# Revit family: Hager-UNIVERS-Surface_mounted-IP44-With_Cover-With_DIN-NoHosted-DE-de
name_source: partatom
category: Electrical Equipment
units: mm (PartAtom-declared; Revit-internal decimal feet)

## family parameters
Always vertical = Yes
Cut with Voids When Loaded = No
Maintain Annotation Orientation = No
Panel Configuration = Two Columns, Circuits Across
Part Type = Panelboard
Room Calculation Point = No
Round Connector Dimension = Use Diameter
Shared = No
Work Plane-Based = Yes

## types (114) — shared parameters
Code hager = ADD-EC000214_EU
Default Elevation = 1200 mm
EF000007 - Farbe = weiß
EF000024 - UV-beständig = No
EF000049 - Tiefe = 165 mm
EF000116 - RAL-Nummer = 9010
EF000118 - Mit Montageplatte = No
EF001062 - EMV-Ausführung = No
EF001088 - Anbaumöglichkeit = Yes
EF001134 - DIN-Schiene = Yes
EF004462 - Art der Schließung = sonstige
EF005474 - Schutzart (IP) = IP44
EF006306 - Mit Schloss = No
EF015941 - Signaldurchlassende Tür = No
ETIM class code = EC000214
ETIM class name = Small distribution board
HG000002-Mit tür = Yes
HG000003-Bereich = UNIVERS
HG000005-Dicke = 2 mm  [stored 0.00656168 ft]
HG000006-Flush mounted = No
HG000011-Leere Reihen von unten = No
HG000012-Türschwenkwinkel = 90.00°
HG000013-Tür links = No
HG000014-Tür rechts = Yes
HG000015-Sichtbarkeit der Türöffnung = Yes
HG000016-3D-Türsichtbarkeit = Yes
HG000017-Distanz zwischen den Polen = 18 mm  [stored 0.0590551 ft]
HG000060-RAL-number = 9010
HG000099-Onfly Template ID-de-DE = 507532
Manufacturer = Hager
Name BIM&CO = Electricity
Name hager = ADD_Enclosures_EC000214
Reference = Template-Enclosure_EU-EC000214
Uniformat = Low Tension Service & Dist.
Uniformat code = D501001
zero-valued in all types: EF001131 - Innentiefe

## per-type parameters (varying)
| type | BC_METADATA | EF000003 - Montageart | EF000008 - Breite | EF000040 - Höhe | EF000218 - Einbautiefe | EF000266 - Anzahl der Reihen | EF000332 - Einbauhöhe | EF000846 - Einbaubreite | EF002950 - Breite in Teilungseinheiten | EF006244 - Transparenter Deckel/Tür | EF009212 - Ausführung Deckel | EF015776 - Erdungsklemmenblock | EF015777 - Neutralleiterklemmenblock | HG000001-Anzahl der Spalten | HG000004-Herstellerreferenz | HG000007-Anzahl der leeren Spalten | HG000008-Anzahl der leeren Reihen | HG000009-Doppelflügeligen Tür | HG000010-Asymmetrische Türen | HGEF000266-Anzahl der Reihen | HGEF0002950-Breite in Teilungseinheiten |
| UNIVERS-Surface_mounted_W800_H1100_D165_36_Modular_Spacing-FWB73 | {"ObjectGuid":"4b98beaf-e054-4bb3-81df-89b0e6f75c23","ModelGuid":"5a9c6bb8-e142-4675-a376-75949bd55e93","VariantGuid":"0dd3dc3a-ebdd-402e-9744-e7fcb90a7f47","Revision":"#6","VariantName":"UNIVERS-Surface_mounted_W800_H1100_D165_36_Modular_Spacing-FWB73"} | Aufputz | 800 mm  [stored 2.62467 ft] | 1100 mm | 161 mm  [stored 0.528215 ft] | 7 | 1100 mm | 800 mm  [stored 2.62467 ft] | 36 | No | mit Ausschnitt | No | Yes | 3 | FWB73 | 0 | 0 | Yes | Yes | 7 | 36 |
| UNIVERS-Surface_mounted_W800_H1100_D165_36_Modular_Spacing-FWB73A | {"ObjectGuid":"4b98beaf-e054-4bb3-81df-89b0e6f75c23","ModelGuid":"5a9c6bb8-e142-4675-a376-75949bd55e93","VariantGuid":"f96014db-38ca-47cd-be6b-f56e55ff9696","Revision":"#6","VariantName":"UNIVERS-Surface_mounted_W800_H1100_D165_36_Modular_Spacing-FWB73A"} | Aufputz | 800 mm  [stored 2.62467 ft] | 1100 mm | 161 mm  [stored 0.528215 ft] | 7 | 1100 mm | 800 mm  [stored 2.62467 ft] | 36 | No | mit Ausschnitt | No | No | 3 | FWB73A | 0 | 0 | Yes | Yes | 7 | 36 |
| UNIVERS-Surface_mounted_W800_H1100_D165_36_Modular_Spacing-FWB73GS | {"ObjectGuid":"4b98beaf-e054-4bb3-81df-89b0e6f75c23","ModelGuid":"5a9c6bb8-e142-4675-a376-75949bd55e93","VariantGuid":"dc065a56-8912-4b0e-b599-fcd4edfbecf9","Revision":"#6","VariantName":"UNIVERS-Surface_mounted_W800_H1100_D165_36_Modular_Spacing-FWB73GS"} | Aufputz | 800 mm  [stored 2.62467 ft] | 1100 mm | 161 mm  [stored 0.528215 ft] | 7 | 1100 mm | 800 mm  [stored 2.62467 ft] | 36 | Yes | mit Ausschnitt | Yes | Yes | 3 | FWB73GS | 0 | 0 | Yes | Yes | 7 | 36 |
| UNIVERS-Surface_mounted_W800_H1100_D165_36_Modular_Spacing-FWB73N | {"ObjectGuid":"4b98beaf-e054-4bb3-81df-89b0e6f75c23","ModelGuid":"5a9c6bb8-e142-4675-a376-75949bd55e93","VariantGuid":"0aaa04c3-c58c-4ad2-b219-bbb140eb05cf","Revision":"#6","VariantName":"UNIVERS-Surface_mounted_W800_H1100_D165_36_Modular_Spacing-FWB73N"} | Aufputz | 800 mm  [stored 2.62467 ft] | 1100 mm | 161 mm  [stored 0.528215 ft] | 7 | 1100 mm | 800 mm  [stored 2.62467 ft] | 36 | No | mit Ausschnitt | No | No | 3 | FWB73N | 0 | 2 | Yes | Yes | 7 | 36 |
| UNIVERS-Surface_mounted_W800_H1100_D165_36_Modular_Spacing-FWB73N3 | {"ObjectGuid":"4b98beaf-e054-4bb3-81df-89b0e6f75c23","ModelGuid":"5a9c6bb8-e142-4675-a376-75949bd55e93","VariantGuid":"30b08112-a314-4a2f-b8eb-9d62cf59b380","Revision":"#6","VariantName":"UNIVERS-Surface_mounted_W800_H1100_D165_36_Modular_Spacing-FWB73N3"} | Aufputz | 800 mm  [stored 2.62467 ft] | 1100 mm | 161 mm  [stored 0.528215 ft] | 7 | 1100 mm | 800 mm  [stored 2.62467 ft] | 36 | No | mit Ausschnitt | No | No | 3 | FWB73N3 | 0 | 2 | Yes | Yes | 7 | 36 |
| UNIVERS-Surface_mounted_W800_H1100_D165_36_Modular_Spacing-FWB73S | {"ObjectGuid":"4b98beaf-e054-4bb3-81df-89b0e6f75c23","ModelGuid":"5a9c6bb8-e142-4675-a376-75949bd55e93","VariantGuid":"13865e0f-bc95-4182-ab0f-007a18ae3678","Revision":"#6","VariantName":"UNIVERS-Surface_mounted_W800_H1100_D165_36_Modular_Spacing-FWB73S"} | Aufputz/Unterputz | 800 mm  [stored 2.62467 ft] | 1100 mm | 161 mm  [stored 0.528215 ft] | 7 | 1100 mm | 800 mm  [stored 2.62467 ft] | 36 | No | mit Ausschnitt | Yes | Yes | 3 | FWB73S | 0 | 0 | Yes | Yes | 7 | 36 |
| UNIVERS-Surface_mounted_W1050_H1100_D165_48_Modular_Spacing-FWB74 | {"ObjectGuid":"4b98beaf-e054-4bb3-81df-89b0e6f75c23","ModelGuid":"5a9c6bb8-e142-4675-a376-75949bd55e93","VariantGuid":"79b8c612-cb7d-4498-8013-b0a4b8235b0e","Revision":"#6","VariantName":"UNIVERS-Surface_mounted_W1050_H1100_D165_48_Modular_Spacing-FWB74"} | Aufputz | 1050 mm | 1100 mm | 161 mm  [stored 0.528215 ft] | 7 | 1100 mm | 1050 mm | 48 | No | mit Ausschnitt | No | Yes | 4 | FWB74 | 0 | 0 | Yes | No | 7 | 48 |
| UNIVERS-Surface_mounted_W1050_H1100_D165_48_Modular_Spacing-FWB74A | {"ObjectGuid":"4b98beaf-e054-4bb3-81df-89b0e6f75c23","ModelGuid":"5a9c6bb8-e142-4675-a376-75949bd55e93","VariantGuid":"296b363e-7e7e-4d48-a850-0f3362c6178a","Revision":"#6","VariantName":"UNIVERS-Surface_mounted_W1050_H1100_D165_48_Modular_Spacing-FWB74A"} | Aufputz | 1050 mm | 1100 mm | 161 mm  [stored 0.528215 ft] | 7 | 1100 mm | 1050 mm | 48 | No | mit Ausschnitt | No | No | 4 | FWB74A | 0 | 0 | Yes | No | 7 | 48 |
| UNIVERS-Surface_mounted_W1050_H1100_D165_48_Modular_Spacing-FWB74GS | {"ObjectGuid":"4b98beaf-e054-4bb3-81df-89b0e6f75c23","ModelGuid":"5a9c6bb8-e142-4675-a376-75949bd55e93","VariantGuid":"3207d950-e017-4842-a3d5-3d6932ddf406","Revision":"#6","VariantName":"UNIVERS-Surface_mounted_W1050_H1100_D165_48_Modular_Spacing-FWB74GS"} | Aufputz | 1050 mm | 1100 mm | 161 mm  [stored 0.528215 ft] | 7 | 1100 mm | 1050 mm | 48 | Yes | mit Ausschnitt | Yes | Yes | 4 | FWB74GS | 0 | 0 | Yes | No | 7 | 48 |
| UNIVERS-Surface_mounted_W1050_H1100_D165_48_Modular_Spacing-FWB74N | {"ObjectGuid":"4b98beaf-e054-4bb3-81df-89b0e6f75c23","ModelGuid":"5a9c6bb8-e142-4675-a376-75949bd55e93","VariantGuid":"8fe7d4e4-44c9-485e-808a-0732e1737a3e","Revision":"#6","VariantName":"UNIVERS-Surface_mounted_W1050_H1100_D165_48_Modular_Spacing-FWB74N"} | Aufputz | 1050 mm | 1100 mm | 161 mm  [stored 0.528215 ft] | 7 | 1100 mm | 1050 mm | 48 | No | mit Ausschnitt | No | No | 4 | FWB74N | 0 | 2 | Yes | No | 7 | 48 |
| UNIVERS-Surface_mounted_W1050_H1100_D165_48_Modular_Spacing-FWB74N3 | {"ObjectGuid":"4b98beaf-e054-4bb3-81df-89b0e6f75c23","ModelGuid":"5a9c6bb8-e142-4675-a376-75949bd55e93","VariantGuid":"1c9d1501-f08c-489e-a837-51ded293aeef","Revision":"#6","VariantName":"UNIVERS-Surface_mounted_W1050_H1100_D165_48_Modular_Spacing-FWB74N3"} | Aufputz | 1050 mm | 1100 mm | 161 mm  [stored 0.528215 ft] | 7 | 1100 mm | 1050 mm | 48 | No | mit Ausschnitt | No | No | 4 | FWB74N3 | 0 | 2 | Yes | No | 7 | 48 |
| UNIVERS-Surface_mounted_W1050_H1100_D165_48_Modular_Spacing-FWB74S | {"ObjectGuid":"4b98beaf-e054-4bb3-81df-89b0e6f75c23","ModelGuid":"5a9c6bb8-e142-4675-a376-75949bd55e93","VariantGuid":"af5bfd4a-45b4-4929-8f2a-3340be27a5a4","Revision":"#6","VariantName":"UNIVERS-Surface_mounted_W1050_H1100_D165_48_Modular_Spacing-FWB74S"} | Aufputz/Unterputz | 1050 mm | 1100 mm | 161 mm  [stored 0.528215 ft] | 7 | 1100 mm | 1050 mm | 48 | No | mit Ausschnitt | Yes | Yes | 4 | FWB74S | 0 | 0 | Yes | No | 7 | 48 |
| UNIVERS-Surface_mounted_W300_H500_D165_12_Modular_Spacing-FWB31 | {"ObjectGuid":"4b98beaf-e054-4bb3-81df-89b0e6f75c23","ModelGuid":"5a9c6bb8-e142-4675-a376-75949bd55e93","VariantGuid":"bc77225f-d96c-479b-8f41-aa01e0b0d45f","Revision":"#6","VariantName":"UNIVERS-Surface_mounted_W300_H500_D165_12_Modular_Spacing-FWB31"} | Aufputz | 300 mm | 500 mm  [stored 1.64042 ft] | 161 mm  [stored 0.528215 ft] | 3 | 500 mm  [stored 1.64042 ft] | 300 mm | 12 | No | mit Ausschnitt | No | Yes | 1 | FWB31 | 0 | 0 | No | No | 3 | 12 |
| UNIVERS-Surface_mounted_W300_H500_D165_12_Modular_Spacing-FWB31A | {"ObjectGuid":"4b98beaf-e054-4bb3-81df-89b0e6f75c23","ModelGuid":"5a9c6bb8-e142-4675-a376-75949bd55e93","VariantGuid":"415a1e9b-bf82-447f-ac86-8f45505e6078","Revision":"#6","VariantName":"UNIVERS-Surface_mounted_W300_H500_D165_12_Modular_Spacing-FWB31A"} | Aufputz | 300 mm | 500 mm  [stored 1.64042 ft] | 161 mm  [stored 0.528215 ft] | 3 | 500 mm  [stored 1.64042 ft] | 300 mm | 12 | No | mit Ausschnitt | No | No | 1 | FWB31A | 0 | 0 | No | No | 3 | 12 |
| UNIVERS-Surface_mounted_W300_H500_D165_12_Modular_Spacing-FWB31GS | {"ObjectGuid":"4b98beaf-e054-4bb3-81df-89b0e6f75c23","ModelGuid":"5a9c6bb8-e142-4675-a376-75949bd55e93","VariantGuid":"e496c8ce-b07f-47c6-9079-46e0f5161702","Revision":"#6","VariantName":"UNIVERS-Surface_mounted_W300_H500_D165_12_Modular_Spacing-FWB31GS"} | Aufputz | 300 mm | 500 mm  [stored 1.64042 ft] | 161 mm  [stored 0.528215 ft] | 3 | 500 mm  [stored 1.64042 ft] | 300 mm | 12 | Yes | mit Ausschnitt | Yes | Yes | 1 | FWB31GS | 0 | 0 | No | No | 3 | 12 |
| UNIVERS-Surface_mounted_W300_H500_D165_12_Modular_Spacing-FWB31P | {"ObjectGuid":"4b98beaf-e054-4bb3-81df-89b0e6f75c23","ModelGuid":"5a9c6bb8-e142-4675-a376-75949bd55e93","VariantGuid":"33e1c743-4a5a-41c3-878c-8eef99396be3","Revision":"#6","VariantName":"UNIVERS-Surface_mounted_W300_H500_D165_12_Modular_Spacing-FWB31P"} | Aufputz | 300 mm | 500 mm  [stored 1.64042 ft] | 161 mm  [stored 0.528215 ft] | 3 | 500 mm  [stored 1.64042 ft] | 300 mm | 12 | No | geschlossen | No | No | 1 | FWB31P | 0 | 0 | No | No | 3 | 12 |
| UNIVERS-Surface_mounted_W300_H500_D165_12_Modular_Spacing-FWB31S | {"ObjectGuid":"4b98beaf-e054-4bb3-81df-89b0e6f75c23","ModelGuid":"5a9c6bb8-e142-4675-a376-75949bd55e93","VariantGuid":"65b11e0e-0d40-4875-a88d-39b95562056d","Revision":"#6","VariantName":"UNIVERS-Surface_mounted_W300_H500_D165_12_Modular_Spacing-FWB31S"} | Aufputz | 300 mm | 500 mm  [stored 1.64042 ft] | 161 mm  [stored 0.528215 ft] | 3 | 500 mm  [stored 1.64042 ft] | 300 mm | 12 | No | mit Ausschnitt | Yes | Yes | 1 | FWB31S | 0 | 0 | No | No | 3 | 12 |
| UNIVERS-Surface_mounted_W550_H500_D165_24_Modular_Spacing-FWB32 | {"ObjectGuid":"4b98beaf-e054-4bb3-81df-89b0e6f75c23","ModelGuid":"5a9c6bb8-e142-4675-a376-75949bd55e93","VariantGuid":"bebb5794-4142-4099-9a25-af55007a6c41","Revision":"#6","VariantName":"UNIVERS-Surface_mounted_W550_H500_D165_24_Modular_Spacing-FWB32"} | Aufputz | 550 mm | 500 mm  [stored 1.64042 ft] | 161 mm  [stored 0.528215 ft] | 3 | 500 mm  [stored 1.64042 ft] | 550 mm | 24 | No | mit Ausschnitt | No | Yes | 2 | FWB32 | 0 | 0 | No | No | 3 | 24 |
| UNIVERS-Surface_mounted_W550_H500_D165_24_Modular_Spacing-FWB32A | {"ObjectGuid":"4b98beaf-e054-4bb3-81df-89b0e6f75c23","ModelGuid":"5a9c6bb8-e142-4675-a376-75949bd55e93","VariantGuid":"89a205b8-98a0-459d-9944-d6146c23cbbf","Revision":"#6","VariantName":"UNIVERS-Surface_mounted_W550_H500_D165_24_Modular_Spacing-FWB32A"} | Aufputz | 550 mm | 500 mm  [stored 1.64042 ft] | 161 mm  [stored 0.528215 ft] | 3 | 500 mm  [stored 1.64042 ft] | 550 mm | 24 | No | mit Ausschnitt | No | No | 2 | FWB32A | 0 | 0 | No | No | 3 | 24 |
| UNIVERS-Surface_mounted_W550_H500_D165_24_Modular_Spacing-FWB32GS | {"ObjectGuid":"4b98beaf-e054-4bb3-81df-89b0e6f75c23","ModelGuid":"5a9c6bb8-e142-4675-a376-75949bd55e93","VariantGuid":"0a3092b4-05a2-4aca-b62c-07ec4acb407b","Revision":"#6","VariantName":"UNIVERS-Surface_mounted_W550_H500_D165_24_Modular_Spacing-FWB32GS"} | Aufputz | 550 mm | 500 mm  [stored 1.64042 ft] | 161 mm  [stored 0.528215 ft] | 3 | 500 mm  [stored 1.64042 ft] | 550 mm | 24 | Yes | mit Ausschnitt | Yes | Yes | 2 | FWB32GS | 0 | 0 | No | No | 3 | 24 |
| UNIVERS-Surface_mounted_W550_H500_D165_24_Modular_Spacing-FWB32P | {"ObjectGuid":"4b98beaf-e054-4bb3-81df-89b0e6f75c23","ModelGuid":"5a9c6bb8-e142-4675-a376-75949bd55e93","VariantGuid":"b824c1df-081b-4e0d-a57e-2454d7213e44","Revision":"#6","VariantName":"UNIVERS-Surface_mounted_W550_H500_D165_24_Modular_Spacing-FWB32P"} | Aufputz | 550 mm | 500 mm  [stored 1.64042 ft] | 161 mm  [stored 0.528215 ft] | 3 | 500 mm  [stored 1.64042 ft] | 550 mm | 24 | No | geschlossen | No | No | 2 | FWB32P | 0 | 0 | No | No | 3 | 24 |
| UNIVERS-Surface_mounted_W550_H500_D165_24_Modular_Spacing-FWB32S | {"ObjectGuid":"4b98beaf-e054-4bb3-81df-89b0e6f75c23","ModelGuid":"5a9c6bb8-e142-4675-a376-75949bd55e93","VariantGuid":"264e37be-930c-46cc-8806-d1fd2ecabab9","Revision":"#6","VariantName":"UNIVERS-Surface_mounted_W550_H500_D165_24_Modular_Spacing-FWB32S"} | Aufputz | 550 mm | 500 mm  [stored 1.64042 ft] | 161 mm  [stored 0.528215 ft] | 3 | 500 mm  [stored 1.64042 ft] | 550 mm | 24 | No | mit Ausschnitt | Yes | Yes | 2 | FWB32S | 0 | 0 | No | No | 3 | 24 |
| UNIVERS-Surface_mounted_W800_H500_D165_36_Modular_Spacing-FWB33 | {"ObjectGuid":"4b98beaf-e054-4bb3-81df-89b0e6f75c23","ModelGuid":"5a9c6bb8-e142-4675-a376-75949bd55e93","VariantGuid":"c96c7007-7639-4225-8408-cc9bf84a3ac0","Revision":"#6","VariantName":"UNIVERS-Surface_mounted_W800_H500_D165_36_Modular_Spacing-FWB33"} | Aufputz | 800 mm  [stored 2.62467 ft] | 500 mm  [stored 1.64042 ft] | 161 mm  [stored 0.528215 ft] | 3 | 500 mm  [stored 1.64042 ft] | 800 mm  [stored 2.62467 ft] | 36 | No | mit Ausschnitt | No | Yes | 3 | FWB33 | 0 | 0 | Yes | Yes | 3 | 36 |
| UNIVERS-Surface_mounted_W800_H500_D165_36_Modular_Spacing-FWB33A | {"ObjectGuid":"4b98beaf-e054-4bb3-81df-89b0e6f75c23","ModelGuid":"5a9c6bb8-e142-4675-a376-75949bd55e93","VariantGuid":"eec06938-f501-4f97-aeb0-44647680a740","Revision":"#6","VariantName":"UNIVERS-Surface_mounted_W800_H500_D165_36_Modular_Spacing-FWB33A"} | Aufputz | 800 mm  [stored 2.62467 ft] | 500 mm  [stored 1.64042 ft] | 161 mm  [stored 0.528215 ft] | 3 | 500 mm  [stored 1.64042 ft] | 800 mm  [stored 2.62467 ft] | 36 | No | mit Ausschnitt | No | No | 3 | FWB33A | 0 | 0 | Yes | Yes | 3 | 36 |
| UNIVERS-Surface_mounted_W800_H500_D165_36_Modular_Spacing-FWB33GS | {"ObjectGuid":"4b98beaf-e054-4bb3-81df-89b0e6f75c23","ModelGuid":"5a9c6bb8-e142-4675-a376-75949bd55e93","VariantGuid":"d985901e-6ba4-4ce1-bd31-d2bd5907da94","Revision":"#6","VariantName":"UNIVERS-Surface_mounted_W800_H500_D165_36_Modular_Spacing-FWB33GS"} | Aufputz | 800 mm  [stored 2.62467 ft] | 500 mm  [stored 1.64042 ft] | 161 mm  [stored 0.528215 ft] | 3 | 500 mm  [stored 1.64042 ft] | 800 mm  [stored 2.62467 ft] | 36 | Yes | mit Ausschnitt | Yes | Yes | 3 | FWB33GS | 0 | 0 | Yes | Yes | 3 | 36 |
| UNIVERS-Surface_mounted_W800_H500_D165_36_Modular_Spacing-FWB33P | {"ObjectGuid":"4b98beaf-e054-4bb3-81df-89b0e6f75c23","ModelGuid":"5a9c6bb8-e142-4675-a376-75949bd55e93","VariantGuid":"7a4ccad5-0dd3-4e05-9244-a928005acc77","Revision":"#6","VariantName":"UNIVERS-Surface_mounted_W800_H500_D165_36_Modular_Spacing-FWB33P"} | Aufputz | 800 mm  [stored 2.62467 ft] | 500 mm  [stored 1.64042 ft] | 161 mm  [stored 0.528215 ft] | 3 | 500 mm  [stored 1.64042 ft] | 800 mm  [stored 2.62467 ft] | 36 | No | mit Ausschnitt | No | No | 3 | FWB33P | 0 | 0 | Yes | Yes | 3 | 36 |
| UNIVERS-Surface_mounted_W800_H500_D165_36_Modular_Spacing-FWB33S | {"ObjectGuid":"4b98beaf-e054-4bb3-81df-89b0e6f75c23","ModelGuid":"5a9c6bb8-e142-4675-a376-75949bd55e93","VariantGuid":"913b1df5-0dcd-47cf-830a-15858840f97b","Revision":"#6","VariantName":"UNIVERS-Surface_mounted_W800_H500_D165_36_Modular_Spacing-FWB33S"} | Aufputz | 800 mm  [stored 2.62467 ft] | 500 mm  [stored 1.64042 ft] | 161 mm  [stored 0.528215 ft] | 3 | 500 mm  [stored 1.64042 ft] | 800 mm  [stored 2.62467 ft] | 36 | No | mit Ausschnitt | Yes | Yes | 3 | FWB33S | 0 | 0 | Yes | Yes | 3 | 36 |
| UNIVERS-Surface_mounted_W1050_H500_D165_48_Modular_Spacing-FWB34 | {"ObjectGuid":"4b98beaf-e054-4bb3-81df-89b0e6f75c23","ModelGuid":"5a9c6bb8-e142-4675-a376-75949bd55e93","VariantGuid":"a5b9a3a1-2cdb-4c4e-8b4d-39d53f138fc0","Revision":"#6","VariantName":"UNIVERS-Surface_mounted_W1050_H500_D165_48_Modular_Spacing-FWB34"} | Aufputz | 1050 mm | 500 mm  [stored 1.64042 ft] | 161 mm  [stored 0.528215 ft] | 3 | 500 mm  [stored 1.64042 ft] | 1050 mm | 48 | No | mit Ausschnitt | No | Yes | 4 | FWB34 | 0 | 0 | Yes | No | 3 | 48 |
| UNIVERS-Surface_mounted_W1050_H500_D165_48_Modular_Spacing-FWB34A | {"ObjectGuid":"4b98beaf-e054-4bb3-81df-89b0e6f75c23","ModelGuid":"5a9c6bb8-e142-4675-a376-75949bd55e93","VariantGuid":"efbc2d72-92be-44ee-880e-fa3157deab8b","Revision":"#6","VariantName":"UNIVERS-Surface_mounted_W1050_H500_D165_48_Modular_Spacing-FWB34A"} | Aufputz | 1050 mm | 500 mm  [stored 1.64042 ft] | 161 mm  [stored 0.528215 ft] | 3 | 500 mm  [stored 1.64042 ft] | 1050 mm | 48 | No | mit Ausschnitt | No | No | 4 | FWB34A | 0 | 0 | Yes | No | 3 | 48 |
| UNIVERS-Surface_mounted_W1050_H500_D165_48_Modular_Spacing-FWB34GS | {"ObjectGuid":"4b98beaf-e054-4bb3-81df-89b0e6f75c23","ModelGuid":"5a9c6bb8-e142-4675-a376-75949bd55e93","VariantGuid":"8a75aa1f-6f37-4399-83e0-a2017874aa32","Revision":"#6","VariantName":"UNIVERS-Surface_mounted_W1050_H500_D165_48_Modular_Spacing-FWB34GS"} | Aufputz | 1050 mm | 500 mm  [stored 1.64042 ft] | 161 mm  [stored 0.528215 ft] | 3 | 500 mm  [stored 1.64042 ft] | 1050 mm | 48 | Yes | mit Ausschnitt | Yes | Yes | 4 | FWB34GS | 0 | 0 | Yes | No | 3 | 48 |
| UNIVERS-Surface_mounted_W1050_H500_D165_48_Modular_Spacing-FWB34P | {"ObjectGuid":"4b98beaf-e054-4bb3-81df-89b0e6f75c23","ModelGuid":"5a9c6bb8-e142-4675-a376-75949bd55e93","VariantGuid":"b6c2c31d-93fb-4289-a6ac-98ff972c8de4","Revision":"#6","VariantName":"UNIVERS-Surface_mounted_W1050_H500_D165_48_Modular_Spacing-FWB34P"} | Aufputz | 1050 mm | 500 mm  [stored 1.64042 ft] | 161 mm  [stored 0.528215 ft] | 3 | 500 mm  [stored 1.64042 ft] | 1050 mm | 48 | No | geschlossen | No | No | 4 | FWB34P | 0 | 0 | Yes | No | 3 | 48 |
| UNIVERS-Surface_mounted_W1050_H500_D165_48_Modular_Spacing-FWB34S | {"ObjectGuid":"4b98beaf-e054-4bb3-81df-89b0e6f75c23","ModelGuid":"5a9c6bb8-e142-4675-a376-75949bd55e93","VariantGuid":"df45b72d-3629-4048-b842-b4b37af0dc65","Revision":"#6","VariantName":"UNIVERS-Surface_mounted_W1050_H500_D165_48_Modular_Spacing-FWB34S"} | Aufputz | 1050 mm | 500 mm  [stored 1.64042 ft] | 161 mm  [stored 0.528215 ft] | 3 | 500 mm  [stored 1.64042 ft] | 1050 mm | 48 | No | mit Ausschnitt | Yes | Yes | 4 | FWB34S | 0 | 0 | Yes | No | 3 | 48 |
| UNIVERS-Surface_mounted_W300_H650_D165_12_Modular_Spacing-FWB41 | {"ObjectGuid":"4b98beaf-e054-4bb3-81df-89b0e6f75c23","ModelGuid":"5a9c6bb8-e142-4675-a376-75949bd55e93","VariantGuid":"45a8b79a-7215-4656-ac70-82b0007d06b8","Revision":"#6","VariantName":"UNIVERS-Surface_mounted_W300_H650_D165_12_Modular_Spacing-FWB41"} | Aufputz | 300 mm | 650 mm  [stored 2.13255 ft] | 161 mm  [stored 0.528215 ft] | 4 | 650 mm  [stored 2.13255 ft] | 300 mm | 12 | No | mit Ausschnitt | No | Yes | 1 | FWB41 | 0 | 0 | No | No | 4 | 12 |
| UNIVERS-Surface_mounted_W300_H650_D165_12_Modular_Spacing-FWB41A | {"ObjectGuid":"4b98beaf-e054-4bb3-81df-89b0e6f75c23","ModelGuid":"5a9c6bb8-e142-4675-a376-75949bd55e93","VariantGuid":"2fc6282c-4443-4830-b9b4-f95fbc1869d7","Revision":"#6","VariantName":"UNIVERS-Surface_mounted_W300_H650_D165_12_Modular_Spacing-FWB41A"} | Aufputz | 300 mm | 650 mm  [stored 2.13255 ft] | 161 mm  [stored 0.528215 ft] | 4 | 650 mm  [stored 2.13255 ft] | 300 mm | 12 | No | mit Ausschnitt | No | No | 1 | FWB41A | 0 | 0 | No | No | 4 | 12 |
| UNIVERS-Surface_mounted_W300_H650_D165_12_Modular_Spacing-FWB41GS | {"ObjectGuid":"4b98beaf-e054-4bb3-81df-89b0e6f75c23","ModelGuid":"5a9c6bb8-e142-4675-a376-75949bd55e93","VariantGuid":"59932cec-805d-41f9-b624-6e9085535888","Revision":"#6","VariantName":"UNIVERS-Surface_mounted_W300_H650_D165_12_Modular_Spacing-FWB41GS"} | Aufputz | 300 mm | 650 mm  [stored 2.13255 ft] | 161 mm  [stored 0.528215 ft] | 4 | 650 mm  [stored 2.13255 ft] | 300 mm | 12 | Yes | mit Ausschnitt | Yes | Yes | 1 | FWB41GS | 0 | 0 | No | No | 4 | 12 |
| UNIVERS-Surface_mounted_W300_H650_D165_12_Modular_Spacing-FWB41P | {"ObjectGuid":"4b98beaf-e054-4bb3-81df-89b0e6f75c23","ModelGuid":"5a9c6bb8-e142-4675-a376-75949bd55e93","VariantGuid":"e2a9a50c-c647-41dc-b70d-1ee2a89a90dd","Revision":"#6","VariantName":"UNIVERS-Surface_mounted_W300_H650_D165_12_Modular_Spacing-FWB41P"} | Aufputz | 300 mm | 650 mm  [stored 2.13255 ft] | 161 mm  [stored 0.528215 ft] | 4 | 650 mm  [stored 2.13255 ft] | 300 mm | 12 | No | geschlossen | No | No | 1 | FWB41P | 0 | 0 | No | No | 4 | 12 |
| UNIVERS-Surface_mounted_W300_H650_D165_12_Modular_Spacing-FWB41S | {"ObjectGuid":"4b98beaf-e054-4bb3-81df-89b0e6f75c23","ModelGuid":"5a9c6bb8-e142-4675-a376-75949bd55e93","VariantGuid":"ceaf870f-a60b-460a-85e5-a4451d4618d1","Revision":"#6","VariantName":"UNIVERS-Surface_mounted_W300_H650_D165_12_Modular_Spacing-FWB41S"} | Aufputz | 300 mm | 650 mm  [stored 2.13255 ft] | 161 mm  [stored 0.528215 ft] | 4 | 650 mm  [stored 2.13255 ft] | 300 mm | 12 | No | mit Ausschnitt | Yes | Yes | 1 | FWB41S | 0 | 0 | No | No | 4 | 12 |
| UNIVERS-Surface_mounted_W550_H650_D165_24_Modular_Spacing-FWB42 | {"ObjectGuid":"4b98beaf-e054-4bb3-81df-89b0e6f75c23","ModelGuid":"5a9c6bb8-e142-4675-a376-75949bd55e93","VariantGuid":"3377098d-3a01-44e4-984c-609051f1b67f","Revision":"#6","VariantName":"UNIVERS-Surface_mounted_W550_H650_D165_24_Modular_Spacing-FWB42"} | Aufputz | 550 mm | 650 mm  [stored 2.13255 ft] | 161 mm  [stored 0.528215 ft] | 4 | 650 mm  [stored 2.13255 ft] | 550 mm | 24 | No | mit Ausschnitt | No | Yes | 2 | FWB42 | 0 | 0 | No | No | 4 | 24 |
| UNIVERS-Surface_mounted_W550_H650_D165_24_Modular_Spacing-FWB42A | {"ObjectGuid":"4b98beaf-e054-4bb3-81df-89b0e6f75c23","ModelGuid":"5a9c6bb8-e142-4675-a376-75949bd55e93","VariantGuid":"6453832f-9356-4162-a701-9e3056fff9f1","Revision":"#6","VariantName":"UNIVERS-Surface_mounted_W550_H650_D165_24_Modular_Spacing-FWB42A"} | Aufputz | 550 mm | 650 mm  [stored 2.13255 ft] | 161 mm  [stored 0.528215 ft] | 4 | 650 mm  [stored 2.13255 ft] | 550 mm | 24 | No | mit Ausschnitt | No | No | 2 | FWB42A | 0 | 0 | No | No | 4 | 24 |
| UNIVERS-Surface_mounted_W550_H650_D165_24_Modular_Spacing-FWB42GS | {"ObjectGuid":"4b98beaf-e054-4bb3-81df-89b0e6f75c23","ModelGuid":"5a9c6bb8-e142-4675-a376-75949bd55e93","VariantGuid":"531e3fc5-d766-47f4-9798-54c22595a34f","Revision":"#6","VariantName":"UNIVERS-Surface_mounted_W550_H650_D165_24_Modular_Spacing-FWB42GS"} | Aufputz | 550 mm | 650 mm  [stored 2.13255 ft] | 161 mm  [stored 0.528215 ft] | 4 | 650 mm  [stored 2.13255 ft] | 550 mm | 24 | Yes | mit Ausschnitt | Yes | Yes | 2 | FWB42GS | 0 | 0 | No | No | 4 | 24 |
| UNIVERS-Surface_mounted_W550_H650_D165_24_Modular_Spacing-FWB42P | {"ObjectGuid":"4b98beaf-e054-4bb3-81df-89b0e6f75c23","ModelGuid":"5a9c6bb8-e142-4675-a376-75949bd55e93","VariantGuid":"6023a988-2405-48a4-862a-0c898c9a6f52","Revision":"#6","VariantName":"UNIVERS-Surface_mounted_W550_H650_D165_24_Modular_Spacing-FWB42P"} | Aufputz | 550 mm | 650 mm  [stored 2.13255 ft] | 161 mm  [stored 0.528215 ft] | 4 | 650 mm  [stored 2.13255 ft] | 550 mm | 24 | No | geschlossen | No | No | 2 | FWB42P | 0 | 0 | No | No | 4 | 24 |
| UNIVERS-Surface_mounted_W550_H650_D165_24_Modular_Spacing-FWB42P2 | {"ObjectGuid":"4b98beaf-e054-4bb3-81df-89b0e6f75c23","ModelGuid":"5a9c6bb8-e142-4675-a376-75949bd55e93","VariantGuid":"f943b17a-2183-4313-ad0f-2ad970ae6d8a","Revision":"#6","VariantName":"UNIVERS-Surface_mounted_W550_H650_D165_24_Modular_Spacing-FWB42P2"} | Aufputz/Unterputz | 550 mm | 650 mm  [stored 2.13255 ft] | 161 mm  [stored 0.528215 ft] | 4 | 650 mm  [stored 2.13255 ft] | 550 mm | 24 | No | mit Ausschnitt | Yes | No | 1 | FWB42P2 | 1 | 0 | No | No | 4 | 24 |
| UNIVERS-Surface_mounted_W550_H650_D165_24_Modular_Spacing-FWB42S | {"ObjectGuid":"4b98beaf-e054-4bb3-81df-89b0e6f75c23","ModelGuid":"5a9c6bb8-e142-4675-a376-75949bd55e93","VariantGuid":"a742818d-e448-49de-a61b-6a587bf37783","Revision":"#6","VariantName":"UNIVERS-Surface_mounted_W550_H650_D165_24_Modular_Spacing-FWB42S"} | Aufputz/Unterputz | 550 mm | 650 mm  [stored 2.13255 ft] | 161 mm  [stored 0.528215 ft] | 4 | 650 mm  [stored 2.13255 ft] | 550 mm | 24 | No | mit Ausschnitt | Yes | Yes | 2 | FWB42S | 0 | 0 | No | No | 4 | 24 |
| UNIVERS-Surface_mounted_W800_H650_D165_36_Modular_Spacing-FWB43 | {"ObjectGuid":"4b98beaf-e054-4bb3-81df-89b0e6f75c23","ModelGuid":"5a9c6bb8-e142-4675-a376-75949bd55e93","VariantGuid":"ffd09cb2-30da-4676-a0bf-1dc946f1099f","Revision":"#6","VariantName":"UNIVERS-Surface_mounted_W800_H650_D165_36_Modular_Spacing-FWB43"} | Aufputz | 800 mm  [stored 2.62467 ft] | 650 mm  [stored 2.13255 ft] | 161 mm  [stored 0.528215 ft] | 4 | 650 mm  [stored 2.13255 ft] | 800 mm  [stored 2.62467 ft] | 36 | No | mit Ausschnitt | No | Yes | 3 | FWB43 | 0 | 0 | Yes | Yes | 4 | 36 |
| UNIVERS-Surface_mounted_W800_H650_D165_36_Modular_Spacing-FWB43A | {"ObjectGuid":"4b98beaf-e054-4bb3-81df-89b0e6f75c23","ModelGuid":"5a9c6bb8-e142-4675-a376-75949bd55e93","VariantGuid":"43dd0842-e84a-4bda-a152-ef60c73ca517","Revision":"#6","VariantName":"UNIVERS-Surface_mounted_W800_H650_D165_36_Modular_Spacing-FWB43A"} | Aufputz | 800 mm  [stored 2.62467 ft] | 650 mm  [stored 2.13255 ft] | 161 mm  [stored 0.528215 ft] | 4 | 650 mm  [stored 2.13255 ft] | 800 mm  [stored 2.62467 ft] | 36 | No | mit Ausschnitt | No | No | 3 | FWB43A | 0 | 0 | Yes | Yes | 4 | 36 |
| UNIVERS-Surface_mounted_W800_H650_D165_36_Modular_Spacing-FWB43GS | {"ObjectGuid":"4b98beaf-e054-4bb3-81df-89b0e6f75c23","ModelGuid":"5a9c6bb8-e142-4675-a376-75949bd55e93","VariantGuid":"adf32a2e-5f2b-459b-8e4c-723d752254ae","Revision":"#6","VariantName":"UNIVERS-Surface_mounted_W800_H650_D165_36_Modular_Spacing-FWB43GS"} | Aufputz | 800 mm  [stored 2.62467 ft] | 650 mm  [stored 2.13255 ft] | 161 mm  [stored 0.528215 ft] | 4 | 650 mm  [stored 2.13255 ft] | 800 mm  [stored 2.62467 ft] | 36 | Yes | mit Ausschnitt | Yes | Yes | 3 | FWB43GS | 0 | 0 | Yes | Yes | 4 | 36 |
| UNIVERS-Surface_mounted_W800_H650_D165_36_Modular_Spacing-FWB43P | {"ObjectGuid":"4b98beaf-e054-4bb3-81df-89b0e6f75c23","ModelGuid":"5a9c6bb8-e142-4675-a376-75949bd55e93","VariantGuid":"be4bf650-8bac-4a14-bc46-b4f3ff1bc119","Revision":"#6","VariantName":"UNIVERS-Surface_mounted_W800_H650_D165_36_Modular_Spacing-FWB43P"} | Aufputz | 800 mm  [stored 2.62467 ft] | 650 mm  [stored 2.13255 ft] | 161 mm  [stored 0.528215 ft] | 4 | 650 mm  [stored 2.13255 ft] | 800 mm  [stored 2.62467 ft] | 36 | No | geschlossen | No | No | 3 | FWB43P | 0 | 0 | Yes | Yes | 4 | 36 |
| UNIVERS-Surface_mounted_W800_H650_D165_36_Modular_Spacing-FWB43S | {"ObjectGuid":"4b98beaf-e054-4bb3-81df-89b0e6f75c23","ModelGuid":"5a9c6bb8-e142-4675-a376-75949bd55e93","VariantGuid":"737b1106-30ae-4983-ac4f-6f9195948b59","Revision":"#6","VariantName":"UNIVERS-Surface_mounted_W800_H650_D165_36_Modular_Spacing-FWB43S"} | Aufputz | 800 mm  [stored 2.62467 ft] | 650 mm  [stored 2.13255 ft] | 161 mm  [stored 0.528215 ft] | 4 | 650 mm  [stored 2.13255 ft] | 800 mm  [stored 2.62467 ft] | 36 | No | mit Ausschnitt | Yes | Yes | 3 | FWB43S | 0 | 0 | Yes | Yes | 4 | 36 |
| UNIVERS-Surface_mounted_W1050_H650_D165_48_Modular_Spacing-FWB44 | {"ObjectGuid":"4b98beaf-e054-4bb3-81df-89b0e6f75c23","ModelGuid":"5a9c6bb8-e142-4675-a376-75949bd55e93","VariantGuid":"141427dd-d9b8-42bd-9a7b-4b53ee938570","Revision":"#6","VariantName":"UNIVERS-Surface_mounted_W1050_H650_D165_48_Modular_Spacing-FWB44"} | Aufputz | 1050 mm | 650 mm  [stored 2.13255 ft] | 161 mm  [stored 0.528215 ft] | 4 | 650 mm  [stored 2.13255 ft] | 1050 mm | 48 | No | mit Ausschnitt | No | Yes | 4 | FWB44 | 0 | 0 | Yes | No | 4 | 48 |
| UNIVERS-Surface_mounted_W1050_H650_D165_48_Modular_Spacing-FWB44A | {"ObjectGuid":"4b98beaf-e054-4bb3-81df-89b0e6f75c23","ModelGuid":"5a9c6bb8-e142-4675-a376-75949bd55e93","VariantGuid":"6e5f6673-953c-4e7e-af0a-7b6d8973f53d","Revision":"#6","VariantName":"UNIVERS-Surface_mounted_W1050_H650_D165_48_Modular_Spacing-FWB44A"} | Aufputz | 1050 mm | 650 mm  [stored 2.13255 ft] | 161 mm  [stored 0.528215 ft] | 4 | 650 mm  [stored 2.13255 ft] | 1050 mm | 48 | No | mit Ausschnitt | No | No | 4 | FWB44A | 0 | 0 | Yes | No | 4 | 48 |
| UNIVERS-Surface_mounted_W1050_H650_D165_48_Modular_Spacing-FWB44GS | {"ObjectGuid":"4b98beaf-e054-4bb3-81df-89b0e6f75c23","ModelGuid":"5a9c6bb8-e142-4675-a376-75949bd55e93","VariantGuid":"e0093d44-6d0a-4141-8bf1-24ed219f4d4a","Revision":"#6","VariantName":"UNIVERS-Surface_mounted_W1050_H650_D165_48_Modular_Spacing-FWB44GS"} | Aufputz | 1050 mm | 650 mm  [stored 2.13255 ft] | 161 mm  [stored 0.528215 ft] | 4 | 650 mm  [stored 2.13255 ft] | 1050 mm | 48 | Yes | mit Ausschnitt | Yes | Yes | 4 | FWB44GS | 0 | 0 | Yes | No | 4 | 48 |
| UNIVERS-Surface_mounted_W1050_H650_D165_48_Modular_Spacing-FWB44P | {"ObjectGuid":"4b98beaf-e054-4bb3-81df-89b0e6f75c23","ModelGuid":"5a9c6bb8-e142-4675-a376-75949bd55e93","VariantGuid":"f3e404c1-b11c-4821-a5f2-8086a3ac6a51","Revision":"#6","VariantName":"UNIVERS-Surface_mounted_W1050_H650_D165_48_Modular_Spacing-FWB44P"} | Aufputz | 1050 mm | 650 mm  [stored 2.13255 ft] | 161 mm  [stored 0.528215 ft] | 4 | 650 mm  [stored 2.13255 ft] | 1050 mm | 48 | No | geschlossen | No | No | 4 | FWB44P | 0 | 0 | Yes | No | 4 | 48 |
| UNIVERS-Surface_mounted_W1050_H650_D165_48_Modular_Spacing-FWB44S | {"ObjectGuid":"4b98beaf-e054-4bb3-81df-89b0e6f75c23","ModelGuid":"5a9c6bb8-e142-4675-a376-75949bd55e93","VariantGuid":"3caea3d7-c083-45d7-8b67-3f4907aae202","Revision":"#6","VariantName":"UNIVERS-Surface_mounted_W1050_H650_D165_48_Modular_Spacing-FWB44S"} | Aufputz | 1050 mm | 650 mm  [stored 2.13255 ft] | 161 mm  [stored 0.528215 ft] | 4 | 650 mm  [stored 2.13255 ft] | 1050 mm | 48 | No | mit Ausschnitt | Yes | Yes | 4 | FWB44S | 0 | 0 | Yes | No | 4 | 48 |
| UNIVERS-Surface_mounted_W300_H800_D165_12_Modular_Spacing-FWB51 | {"ObjectGuid":"4b98beaf-e054-4bb3-81df-89b0e6f75c23","ModelGuid":"5a9c6bb8-e142-4675-a376-75949bd55e93","VariantGuid":"cde8fc30-e85d-475f-b0da-f0d0555d50cc","Revision":"#6","VariantName":"UNIVERS-Surface_mounted_W300_H800_D165_12_Modular_Spacing-FWB51"} | Aufputz | 300 mm | 800 mm  [stored 2.62467 ft] | 161 mm  [stored 0.528215 ft] | 5 | 800 mm  [stored 2.62467 ft] | 300 mm | 12 | No | mit Ausschnitt | No | Yes | 1 | FWB51 | 0 | 0 | No | No | 5 | 12 |
| UNIVERS-Surface_mounted_W300_H800_D165_12_Modular_Spacing-FWB51A | {"ObjectGuid":"4b98beaf-e054-4bb3-81df-89b0e6f75c23","ModelGuid":"5a9c6bb8-e142-4675-a376-75949bd55e93","VariantGuid":"efe3270c-161a-4a4a-8804-e1901b716d65","Revision":"#6","VariantName":"UNIVERS-Surface_mounted_W300_H800_D165_12_Modular_Spacing-FWB51A"} | Aufputz | 300 mm | 800 mm  [stored 2.62467 ft] | 161 mm  [stored 0.528215 ft] | 5 | 800 mm  [stored 2.62467 ft] | 300 mm | 12 | No | mit Ausschnitt | No | No | 1 | FWB51A | 0 | 0 | No | No | 5 | 12 |
| UNIVERS-Surface_mounted_W300_H800_D165_12_Modular_Spacing-FWB51GS | {"ObjectGuid":"4b98beaf-e054-4bb3-81df-89b0e6f75c23","ModelGuid":"5a9c6bb8-e142-4675-a376-75949bd55e93","VariantGuid":"c923d242-e13f-444e-bcf4-43b74442c37b","Revision":"#6","VariantName":"UNIVERS-Surface_mounted_W300_H800_D165_12_Modular_Spacing-FWB51GS"} | Aufputz | 300 mm | 800 mm  [stored 2.62467 ft] | 161 mm  [stored 0.528215 ft] | 5 | 800 mm  [stored 2.62467 ft] | 300 mm | 12 | Yes | mit Ausschnitt | Yes | Yes | 1 | FWB51GS | 0 | 0 | No | No | 5 | 12 |
| UNIVERS-Surface_mounted_W300_H800_D165_12_Modular_Spacing-FWB51P | {"ObjectGuid":"4b98beaf-e054-4bb3-81df-89b0e6f75c23","ModelGuid":"5a9c6bb8-e142-4675-a376-75949bd55e93","VariantGuid":"138c7fe6-c990-4b29-a0a6-085476861516","Revision":"#6","VariantName":"UNIVERS-Surface_mounted_W300_H800_D165_12_Modular_Spacing-FWB51P"} | Aufputz | 300 mm | 800 mm  [stored 2.62467 ft] | 161 mm  [stored 0.528215 ft] | 5 | 800 mm  [stored 2.62467 ft] | 300 mm | 12 | No | geschlossen | No | No | 1 | FWB51P | 0 | 0 | No | No | 5 | 12 |
| UNIVERS-Surface_mounted_W300_H800_D165_12_Modular_Spacing-FWB51S | {"ObjectGuid":"4b98beaf-e054-4bb3-81df-89b0e6f75c23","ModelGuid":"5a9c6bb8-e142-4675-a376-75949bd55e93","VariantGuid":"0fc9e1a8-7adf-4268-8bfd-e8e6263bf6c0","Revision":"#6","VariantName":"UNIVERS-Surface_mounted_W300_H800_D165_12_Modular_Spacing-FWB51S"} | Aufputz | 300 mm | 800 mm  [stored 2.62467 ft] | 161 mm  [stored 0.528215 ft] | 5 | 800 mm  [stored 2.62467 ft] | 300 mm | 12 | No | mit Ausschnitt | Yes | Yes | 1 | FWB51S | 0 | 0 | No | No | 5 | 12 |
| UNIVERS-Surface_mounted_W550_H800_D165_24_Modular_Spacing-FWB52 | {"ObjectGuid":"4b98beaf-e054-4bb3-81df-89b0e6f75c23","ModelGuid":"5a9c6bb8-e142-4675-a376-75949bd55e93","VariantGuid":"8950b0d1-f4ff-4cce-ba0c-da24363e133f","Revision":"#6","VariantName":"UNIVERS-Surface_mounted_W550_H800_D165_24_Modular_Spacing-FWB52"} | Aufputz | 550 mm | 800 mm  [stored 2.62467 ft] | 161 mm  [stored 0.528215 ft] | 5 | 800 mm  [stored 2.62467 ft] | 550 mm | 24 | No | mit Ausschnitt | No | Yes | 2 | FWB52 | 0 | 0 | No | No | 5 | 24 |
| UNIVERS-Surface_mounted_W550_H800_D165_24_Modular_Spacing-FWB52A | {"ObjectGuid":"4b98beaf-e054-4bb3-81df-89b0e6f75c23","ModelGuid":"5a9c6bb8-e142-4675-a376-75949bd55e93","VariantGuid":"7606d88a-15e4-430b-96e9-25c2aea0cfdf","Revision":"#6","VariantName":"UNIVERS-Surface_mounted_W550_H800_D165_24_Modular_Spacing-FWB52A"} | Aufputz | 550 mm | 800 mm  [stored 2.62467 ft] | 161 mm  [stored 0.528215 ft] | 5 | 800 mm  [stored 2.62467 ft] | 550 mm | 24 | No | mit Ausschnitt | No | No | 2 | FWB52A | 0 | 0 | No | No | 5 | 24 |
| UNIVERS-Surface_mounted_W550_H800_D165_24_Modular_Spacing-FWB52GS | {"ObjectGuid":"4b98beaf-e054-4bb3-81df-89b0e6f75c23","ModelGuid":"5a9c6bb8-e142-4675-a376-75949bd55e93","VariantGuid":"bd06cbc2-40cc-48ee-bf33-7d83b8b2920e","Revision":"#6","VariantName":"UNIVERS-Surface_mounted_W550_H800_D165_24_Modular_Spacing-FWB52GS"} | Aufputz | 550 mm | 800 mm  [stored 2.62467 ft] | 161 mm  [stored 0.528215 ft] | 5 | 800 mm  [stored 2.62467 ft] | 550 mm | 24 | Yes | mit Ausschnitt | Yes | Yes | 2 | FWB52GS | 0 | 0 | No | No | 5 | 24 |
| UNIVERS-Surface_mounted_W550_H800_D165_24_Modular_Spacing-FWB52N | {"ObjectGuid":"4b98beaf-e054-4bb3-81df-89b0e6f75c23","ModelGuid":"5a9c6bb8-e142-4675-a376-75949bd55e93","VariantGuid":"1f83655f-060a-41e3-a9cc-76c672a5d63a","Revision":"#6","VariantName":"UNIVERS-Surface_mounted_W550_H800_D165_24_Modular_Spacing-FWB52N"} | Aufputz | 550 mm | 800 mm  [stored 2.62467 ft] | 161 mm  [stored 0.528215 ft] | 5 | 800 mm  [stored 2.62467 ft] | 550 mm | 24 | No | mit Ausschnitt | No | No | 2 | FWB52N | 0 | 2 | No | No | 5 | 24 |
| UNIVERS-Surface_mounted_W550_H800_D165_24_Modular_Spacing-FWB52N3 | {"ObjectGuid":"4b98beaf-e054-4bb3-81df-89b0e6f75c23","ModelGuid":"5a9c6bb8-e142-4675-a376-75949bd55e93","VariantGuid":"9c0c2fe8-33bb-432e-b5ad-358df6d21266","Revision":"#6","VariantName":"UNIVERS-Surface_mounted_W550_H800_D165_24_Modular_Spacing-FWB52N3"} | Aufputz | 550 mm | 800 mm  [stored 2.62467 ft] | 160 mm  [stored 0.524934 ft] | 5 | 800 mm  [stored 2.62467 ft] | 550 mm | 24 | No | mit Ausschnitt | No | No | 2 | FWB52N3 | 0 | 2 | No | No | 5 | 24 |
| UNIVERS-Surface_mounted_W550_H800_D165_24_Modular_Spacing-FWB52P | {"ObjectGuid":"4b98beaf-e054-4bb3-81df-89b0e6f75c23","ModelGuid":"5a9c6bb8-e142-4675-a376-75949bd55e93","VariantGuid":"67b31392-898f-4e61-a6f7-fa329ca3a347","Revision":"#6","VariantName":"UNIVERS-Surface_mounted_W550_H800_D165_24_Modular_Spacing-FWB52P"} | Aufputz | 550 mm | 800 mm  [stored 2.62467 ft] | 161 mm  [stored 0.528215 ft] | 5 | 800 mm  [stored 2.62467 ft] | 550 mm | 24 | No | geschlossen | No | No | 2 | FWB52P | 0 | 0 | No | No | 5 | 24 |
| UNIVERS-Surface_mounted_W550_H800_D165_24_Modular_Spacing-FWB52P2 | {"ObjectGuid":"4b98beaf-e054-4bb3-81df-89b0e6f75c23","ModelGuid":"5a9c6bb8-e142-4675-a376-75949bd55e93","VariantGuid":"c945316e-b23e-4bf7-9d44-a47a7ab19e73","Revision":"#6","VariantName":"UNIVERS-Surface_mounted_W550_H800_D165_24_Modular_Spacing-FWB52P2"} | Aufputz/Unterputz | 550 mm | 800 mm  [stored 2.62467 ft] | 161 mm  [stored 0.528215 ft] | 5 | 800 mm  [stored 2.62467 ft] | 550 mm | 24 | No | mit Ausschnitt | Yes | No | 1 | FWB52P2 | 1 | 0 | No | No | 5 | 24 |
| UNIVERS-Surface_mounted_W550_H800_D165_24_Modular_Spacing-FWB52S | {"ObjectGuid":"4b98beaf-e054-4bb3-81df-89b0e6f75c23","ModelGuid":"5a9c6bb8-e142-4675-a376-75949bd55e93","VariantGuid":"5b10f517-9eb5-4358-86a0-2d34eecb0dc0","Revision":"#6","VariantName":"UNIVERS-Surface_mounted_W550_H800_D165_24_Modular_Spacing-FWB52S"} | Aufputz | 550 mm | 800 mm  [stored 2.62467 ft] | 161 mm  [stored 0.528215 ft] | 5 | 800 mm  [stored 2.62467 ft] | 550 mm | 24 | No | mit Ausschnitt | Yes | Yes | 2 | FWB52S | 0 | 0 | No | No | 5 | 24 |
| UNIVERS-Surface_mounted_W800_H800_D165_36_Modular_Spacing-FWB53 | {"ObjectGuid":"4b98beaf-e054-4bb3-81df-89b0e6f75c23","ModelGuid":"5a9c6bb8-e142-4675-a376-75949bd55e93","VariantGuid":"2af88a2d-daf2-4cd3-8a1f-9c795d38301d","Revision":"#6","VariantName":"UNIVERS-Surface_mounted_W800_H800_D165_36_Modular_Spacing-FWB53"} | Aufputz | 800 mm  [stored 2.62467 ft] | 800 mm  [stored 2.62467 ft] | 161 mm  [stored 0.528215 ft] | 5 | 800 mm  [stored 2.62467 ft] | 800 mm  [stored 2.62467 ft] | 36 | No | mit Ausschnitt | No | Yes | 3 | FWB53 | 0 | 0 | Yes | Yes | 5 | 36 |
| UNIVERS-Surface_mounted_W800_H800_D165_36_Modular_Spacing-FWB53A | {"ObjectGuid":"4b98beaf-e054-4bb3-81df-89b0e6f75c23","ModelGuid":"5a9c6bb8-e142-4675-a376-75949bd55e93","VariantGuid":"4013537c-ed17-4622-85c8-3cebded502a9","Revision":"#6","VariantName":"UNIVERS-Surface_mounted_W800_H800_D165_36_Modular_Spacing-FWB53A"} | Aufputz | 800 mm  [stored 2.62467 ft] | 800 mm  [stored 2.62467 ft] | 161 mm  [stored 0.528215 ft] | 5 | 800 mm  [stored 2.62467 ft] | 800 mm  [stored 2.62467 ft] | 36 | No | mit Ausschnitt | No | No | 3 | FWB53A | 0 | 0 | Yes | Yes | 5 | 36 |
| UNIVERS-Surface_mounted_W800_H800_D165_36_Modular_Spacing-FWB53GS | {"ObjectGuid":"4b98beaf-e054-4bb3-81df-89b0e6f75c23","ModelGuid":"5a9c6bb8-e142-4675-a376-75949bd55e93","VariantGuid":"5ce05ccd-e6cb-4540-bc1b-4ba7c9a05c89","Revision":"#6","VariantName":"UNIVERS-Surface_mounted_W800_H800_D165_36_Modular_Spacing-FWB53GS"} | Aufputz | 800 mm  [stored 2.62467 ft] | 800 mm  [stored 2.62467 ft] | 161 mm  [stored 0.528215 ft] | 5 | 800 mm  [stored 2.62467 ft] | 800 mm  [stored 2.62467 ft] | 36 | Yes | mit Ausschnitt | Yes | Yes | 3 | FWB53GS | 0 | 0 | Yes | Yes | 5 | 36 |
| UNIVERS-Surface_mounted_W800_H800_D165_36_Modular_Spacing-FWB53N | {"ObjectGuid":"4b98beaf-e054-4bb3-81df-89b0e6f75c23","ModelGuid":"5a9c6bb8-e142-4675-a376-75949bd55e93","VariantGuid":"52fd4958-bdd8-4fdd-9510-ec8e62447174","Revision":"#6","VariantName":"UNIVERS-Surface_mounted_W800_H800_D165_36_Modular_Spacing-FWB53N"} | Aufputz | 800 mm  [stored 2.62467 ft] | 800 mm  [stored 2.62467 ft] | 161 mm  [stored 0.528215 ft] | 5 | 800 mm  [stored 2.62467 ft] | 800 mm  [stored 2.62467 ft] | 36 | No | mit Ausschnitt | No | No | 3 | FWB53N | 0 | 2 | Yes | Yes | 5 | 36 |
| UNIVERS-Surface_mounted_W800_H800_D165_36_Modular_Spacing-FWB53N3 | {"ObjectGuid":"4b98beaf-e054-4bb3-81df-89b0e6f75c23","ModelGuid":"5a9c6bb8-e142-4675-a376-75949bd55e93","VariantGuid":"a61a3efc-82bc-4810-bd19-907cac2a4ab5","Revision":"#6","VariantName":"UNIVERS-Surface_mounted_W800_H800_D165_36_Modular_Spacing-FWB53N3"} | Aufputz | 800 mm  [stored 2.62467 ft] | 800 mm  [stored 2.62467 ft] | 161 mm  [stored 0.528215 ft] | 5 | 800 mm  [stored 2.62467 ft] | 800 mm  [stored 2.62467 ft] | 36 | No | mit Ausschnitt | No | No | 3 | FWB53N3 | 0 | 2 | Yes | Yes | 5 | 36 |
| UNIVERS-Surface_mounted_W800_H800_D165_36_Modular_Spacing-FWB53P | {"ObjectGuid":"4b98beaf-e054-4bb3-81df-89b0e6f75c23","ModelGuid":"5a9c6bb8-e142-4675-a376-75949bd55e93","VariantGuid":"461638e4-e26a-4f49-b55e-422e2c70fbd4","Revision":"#6","VariantName":"UNIVERS-Surface_mounted_W800_H800_D165_36_Modular_Spacing-FWB53P"} | Aufputz | 800 mm  [stored 2.62467 ft] | 800 mm  [stored 2.62467 ft] | 161 mm  [stored 0.528215 ft] | 5 | 800 mm  [stored 2.62467 ft] | 800 mm  [stored 2.62467 ft] | 36 | No | geschlossen | No | No | 3 | FWB53P | 0 | 0 | Yes | No | 5 | 36 |
| UNIVERS-Surface_mounted_W800_H800_D165_36_Modular_Spacing-FWB53S | {"ObjectGuid":"4b98beaf-e054-4bb3-81df-89b0e6f75c23","ModelGuid":"5a9c6bb8-e142-4675-a376-75949bd55e93","VariantGuid":"3ea8a96e-d647-441f-9334-d18083b86931","Revision":"#6","VariantName":"UNIVERS-Surface_mounted_W800_H800_D165_36_Modular_Spacing-FWB53S"} | Aufputz | 800 mm  [stored 2.62467 ft] | 800 mm  [stored 2.62467 ft] | 161 mm  [stored 0.528215 ft] | 5 | 800 mm  [stored 2.62467 ft] | 800 mm  [stored 2.62467 ft] | 36 | No | mit Ausschnitt | Yes | Yes | 3 | FWB53S | 0 | 0 | Yes | Yes | 5 | 36 |
| UNIVERS-Surface_mounted_W1050_H800_D165_48_Modular_Spacing-FWB54 | {"ObjectGuid":"4b98beaf-e054-4bb3-81df-89b0e6f75c23","ModelGuid":"5a9c6bb8-e142-4675-a376-75949bd55e93","VariantGuid":"be478a6f-2a58-43cb-a412-aea2857449e0","Revision":"#6","VariantName":"UNIVERS-Surface_mounted_W1050_H800_D165_48_Modular_Spacing-FWB54"} | Aufputz | 1050 mm | 800 mm  [stored 2.62467 ft] | 161 mm  [stored 0.528215 ft] | 5 | 800 mm  [stored 2.62467 ft] | 1050 mm | 48 | No | mit Ausschnitt | No | Yes | 4 | FWB54 | 0 | 0 | Yes | No | 5 | 48 |
| UNIVERS-Surface_mounted_W1050_H800_D165_48_Modular_Spacing-FWB54A | {"ObjectGuid":"4b98beaf-e054-4bb3-81df-89b0e6f75c23","ModelGuid":"5a9c6bb8-e142-4675-a376-75949bd55e93","VariantGuid":"b5dc7b0a-4906-413b-b4f1-390d6a432d97","Revision":"#6","VariantName":"UNIVERS-Surface_mounted_W1050_H800_D165_48_Modular_Spacing-FWB54A"} | Aufputz | 1050 mm | 800 mm  [stored 2.62467 ft] | 161 mm  [stored 0.528215 ft] | 5 | 800 mm  [stored 2.62467 ft] | 1050 mm | 48 | No | mit Ausschnitt | No | No | 4 | FWB54A | 0 | 0 | Yes | No | 5 | 48 |
| UNIVERS-Surface_mounted_W1050_H800_D165_48_Modular_Spacing-FWB54GS | {"ObjectGuid":"4b98beaf-e054-4bb3-81df-89b0e6f75c23","ModelGuid":"5a9c6bb8-e142-4675-a376-75949bd55e93","VariantGuid":"c6a204ec-355d-4e88-82c3-85ee1c2c9717","Revision":"#6","VariantName":"UNIVERS-Surface_mounted_W1050_H800_D165_48_Modular_Spacing-FWB54GS"} | Aufputz | 1050 mm | 800 mm  [stored 2.62467 ft] | 161 mm  [stored 0.528215 ft] | 5 | 800 mm  [stored 2.62467 ft] | 1050 mm | 48 | Yes | mit Ausschnitt | Yes | Yes | 4 | FWB54GS | 0 | 0 | Yes | No | 5 | 48 |
| UNIVERS-Surface_mounted_W1050_H800_D165_48_Modular_Spacing-FWB54P | {"ObjectGuid":"4b98beaf-e054-4bb3-81df-89b0e6f75c23","ModelGuid":"5a9c6bb8-e142-4675-a376-75949bd55e93","VariantGuid":"44f79640-85ce-4d68-9154-ea6963289d0c","Revision":"#6","VariantName":"UNIVERS-Surface_mounted_W1050_H800_D165_48_Modular_Spacing-FWB54P"} | Aufputz | 1050 mm | 800 mm  [stored 2.62467 ft] | 161 mm  [stored 0.528215 ft] | 5 | 800 mm  [stored 2.62467 ft] | 1050 mm | 48 | No | geschlossen | No | No | 4 | FWB54P | 0 | 0 | Yes | No | 5 | 48 |
| UNIVERS-Surface_mounted_W1050_H800_D165_48_Modular_Spacing-FWB54S | {"ObjectGuid":"4b98beaf-e054-4bb3-81df-89b0e6f75c23","ModelGuid":"5a9c6bb8-e142-4675-a376-75949bd55e93","VariantGuid":"e22d619d-f2e5-44ec-835a-e05814a1c68c","Revision":"#6","VariantName":"UNIVERS-Surface_mounted_W1050_H800_D165_48_Modular_Spacing-FWB54S"} | Aufputz | 1050 mm | 800 mm  [stored 2.62467 ft] | 161 mm  [stored 0.528215 ft] | 5 | 800 mm  [stored 2.62467 ft] | 1050 mm | 48 | No | mit Ausschnitt | Yes | Yes | 4 | FWB54S | 0 | 0 | Yes | No | 5 | 48 |
| UNIVERS-Surface_mounted_W300_H950_D165_12_Modular_Spacing-FWB61 | {"ObjectGuid":"4b98beaf-e054-4bb3-81df-89b0e6f75c23","ModelGuid":"5a9c6bb8-e142-4675-a376-75949bd55e93","VariantGuid":"d2bde084-cd77-4a94-8dbb-97af9eaa7a93","Revision":"#6","VariantName":"UNIVERS-Surface_mounted_W300_H950_D165_12_Modular_Spacing-FWB61"} | Aufputz | 300 mm | 950 mm  [stored 3.1168 ft] | 161 mm  [stored 0.528215 ft] | 6 | 950 mm  [stored 3.1168 ft] | 300 mm | 12 | No | mit Ausschnitt | No | Yes | 1 | FWB61 | 0 | 0 | No | No | 6 | 12 |
| UNIVERS-Surface_mounted_W300_H950_D165_12_Modular_Spacing-FWB61A | {"ObjectGuid":"4b98beaf-e054-4bb3-81df-89b0e6f75c23","ModelGuid":"5a9c6bb8-e142-4675-a376-75949bd55e93","VariantGuid":"fda06cc3-f1ea-4b16-bec6-c79be4a74ae9","Revision":"#6","VariantName":"UNIVERS-Surface_mounted_W300_H950_D165_12_Modular_Spacing-FWB61A"} | Aufputz | 300 mm | 950 mm  [stored 3.1168 ft] | 161 mm  [stored 0.528215 ft] | 6 | 950 mm  [stored 3.1168 ft] | 300 mm | 12 | No | mit Ausschnitt | No | No | 1 | FWB61A | 0 | 0 | No | No | 6 | 12 |
| UNIVERS-Surface_mounted_W300_H950_D165_12_Modular_Spacing-FWB61GS | {"ObjectGuid":"4b98beaf-e054-4bb3-81df-89b0e6f75c23","ModelGuid":"5a9c6bb8-e142-4675-a376-75949bd55e93","VariantGuid":"acd9f76f-6e39-4b30-bdbe-237fd4e123a2","Revision":"#6","VariantName":"UNIVERS-Surface_mounted_W300_H950_D165_12_Modular_Spacing-FWB61GS"} | Aufputz | 300 mm | 950 mm  [stored 3.1168 ft] | 161 mm  [stored 0.528215 ft] | 6 | 950 mm  [stored 3.1168 ft] | 300 mm | 12 | Yes | mit Ausschnitt | Yes | Yes | 1 | FWB61GS | 0 | 0 | No | No | 6 | 12 |
| UNIVERS-Surface_mounted_W300_H950_D165_12_Modular_Spacing-FWB61P | {"ObjectGuid":"4b98beaf-e054-4bb3-81df-89b0e6f75c23","ModelGuid":"5a9c6bb8-e142-4675-a376-75949bd55e93","VariantGuid":"38fa070f-ceb1-4e04-b511-03a1cb744e46","Revision":"#6","VariantName":"UNIVERS-Surface_mounted_W300_H950_D165_12_Modular_Spacing-FWB61P"} | Aufputz | 300 mm | 950 mm  [stored 3.1168 ft] | 161 mm  [stored 0.528215 ft] | 6 | 950 mm  [stored 3.1168 ft] | 300 mm | 12 | No | geschlossen | No | No | 1 | FWB61P | 0 | 0 | No | No | 6 | 12 |
| UNIVERS-Surface_mounted_W300_H950_D165_12_Modular_Spacing-FWB61S | {"ObjectGuid":"4b98beaf-e054-4bb3-81df-89b0e6f75c23","ModelGuid":"5a9c6bb8-e142-4675-a376-75949bd55e93","VariantGuid":"0d3b0a9c-ba8f-4a55-b2da-565554299442","Revision":"#6","VariantName":"UNIVERS-Surface_mounted_W300_H950_D165_12_Modular_Spacing-FWB61S"} | Aufputz | 300 mm | 950 mm  [stored 3.1168 ft] | 161 mm  [stored 0.528215 ft] | 6 | 950 mm  [stored 3.1168 ft] | 300 mm | 12 | No | mit Ausschnitt | Yes | Yes | 1 | FWB61S | 0 | 0 | No | No | 6 | 12 |
| UNIVERS-Surface_mounted_W550_H950_D165_24_Modular_Spacing-FWB62 | {"ObjectGuid":"4b98beaf-e054-4bb3-81df-89b0e6f75c23","ModelGuid":"5a9c6bb8-e142-4675-a376-75949bd55e93","VariantGuid":"af110a8b-dd36-49f9-b204-d718fb91ef79","Revision":"#6","VariantName":"UNIVERS-Surface_mounted_W550_H950_D165_24_Modular_Spacing-FWB62"} | Aufputz | 550 mm | 950 mm  [stored 3.1168 ft] | 161 mm  [stored 0.528215 ft] | 6 | 950 mm  [stored 3.1168 ft] | 550 mm | 24 | No | mit Ausschnitt | No | Yes | 2 | FWB62 | 0 | 0 | No | No | 6 | 24 |
| UNIVERS-Surface_mounted_W550_H950_D165_24_Modular_Spacing-FWB62A | {"ObjectGuid":"4b98beaf-e054-4bb3-81df-89b0e6f75c23","ModelGuid":"5a9c6bb8-e142-4675-a376-75949bd55e93","VariantGuid":"9ec738d6-7f14-45e0-a9ee-91050ed07e3f","Revision":"#6","VariantName":"UNIVERS-Surface_mounted_W550_H950_D165_24_Modular_Spacing-FWB62A"} | Aufputz | 550 mm | 950 mm  [stored 3.1168 ft] | 161 mm  [stored 0.528215 ft] | 6 | 950 mm  [stored 3.1168 ft] | 550 mm | 24 | No | mit Ausschnitt | No | No | 2 | FWB62A | 0 | 0 | No | No | 6 | 24 |
| UNIVERS-Surface_mounted_W550_H950_D165_24_Modular_Spacing-FWB62GS | {"ObjectGuid":"4b98beaf-e054-4bb3-81df-89b0e6f75c23","ModelGuid":"5a9c6bb8-e142-4675-a376-75949bd55e93","VariantGuid":"c83c189f-ca80-478d-b35f-49119ccf5fcc","Revision":"#6","VariantName":"UNIVERS-Surface_mounted_W550_H950_D165_24_Modular_Spacing-FWB62GS"} | Aufputz | 550 mm | 950 mm  [stored 3.1168 ft] | 161 mm  [stored 0.528215 ft] | 6 | 950 mm  [stored 3.1168 ft] | 550 mm | 24 | Yes | mit Ausschnitt | Yes | Yes | 2 | FWB62GS | 0 | 0 | No | No | 6 | 24 |
| UNIVERS-Surface_mounted_W550_H950_D165_24_Modular_Spacing-FWB62N | {"ObjectGuid":"4b98beaf-e054-4bb3-81df-89b0e6f75c23","ModelGuid":"5a9c6bb8-e142-4675-a376-75949bd55e93","VariantGuid":"5c0f4a89-757e-4865-8a06-adb010fe54c1","Revision":"#6","VariantName":"UNIVERS-Surface_mounted_W550_H950_D165_24_Modular_Spacing-FWB62N"} | Aufputz | 550 mm | 950 mm  [stored 3.1168 ft] | 161 mm  [stored 0.528215 ft] | 6 | 950 mm  [stored 3.1168 ft] | 550 mm | 24 | No | mit Ausschnitt | No | No | 2 | FWB62N | 0 | 2 | No | No | 6 | 24 |
| UNIVERS-Surface_mounted_W550_H950_D165_24_Modular_Spacing-FWB62N3 | {"ObjectGuid":"4b98beaf-e054-4bb3-81df-89b0e6f75c23","ModelGuid":"5a9c6bb8-e142-4675-a376-75949bd55e93","VariantGuid":"982818f3-f735-447d-887b-cca19d5d50a7","Revision":"#6","VariantName":"UNIVERS-Surface_mounted_W550_H950_D165_24_Modular_Spacing-FWB62N3"} | Aufputz | 550 mm | 950 mm  [stored 3.1168 ft] | 161 mm  [stored 0.528215 ft] | 6 | 950 mm  [stored 3.1168 ft] | 550 mm | 24 | No | mit Ausschnitt | No | No | 2 | FWB62N3 | 0 | 2 | No | No | 6 | 24 |
| UNIVERS-Surface_mounted_W550_H950_D165_24_Modular_Spacing-FWB62P | {"ObjectGuid":"4b98beaf-e054-4bb3-81df-89b0e6f75c23","ModelGuid":"5a9c6bb8-e142-4675-a376-75949bd55e93","VariantGuid":"040fc1db-162b-4ca2-b175-667a8951ead8","Revision":"#6","VariantName":"UNIVERS-Surface_mounted_W550_H950_D165_24_Modular_Spacing-FWB62P"} | Aufputz | 550 mm | 950 mm  [stored 3.1168 ft] | 161 mm  [stored 0.528215 ft] | 6 | 950 mm  [stored 3.1168 ft] | 550 mm | 24 | No | geschlossen | No | No | 2 | FWB62P | 0 | 0 | No | No | 6 | 24 |
| UNIVERS-Surface_mounted_W550_H950_D165_24_Modular_Spacing-FWB62S | {"ObjectGuid":"4b98beaf-e054-4bb3-81df-89b0e6f75c23","ModelGuid":"5a9c6bb8-e142-4675-a376-75949bd55e93","VariantGuid":"f3cd2511-c6ce-46b5-b789-edaf1e540073","Revision":"#6","VariantName":"UNIVERS-Surface_mounted_W550_H950_D165_24_Modular_Spacing-FWB62S"} | Aufputz | 550 mm | 950 mm  [stored 3.1168 ft] | 161 mm  [stored 0.528215 ft] | 6 | 950 mm  [stored 3.1168 ft] | 550 mm | 24 | No | mit Ausschnitt | Yes | Yes | 2 | FWB62S | 0 | 0 | No | No | 6 | 24 |
| UNIVERS-Surface_mounted_W800_H950_D165_36_Modular_Spacing-FWB63 | {"ObjectGuid":"4b98beaf-e054-4bb3-81df-89b0e6f75c23","ModelGuid":"5a9c6bb8-e142-4675-a376-75949bd55e93","VariantGuid":"85484e44-5d86-4b07-8d58-b34eb632f497","Revision":"#6","VariantName":"UNIVERS-Surface_mounted_W800_H950_D165_36_Modular_Spacing-FWB63"} | Aufputz | 800 mm  [stored 2.62467 ft] | 950 mm  [stored 3.1168 ft] | 161 mm  [stored 0.528215 ft] | 6 | 950 mm  [stored 3.1168 ft] | 800 mm  [stored 2.62467 ft] | 36 | No | mit Ausschnitt | No | Yes | 3 | FWB63 | 0 | 0 | Yes | Yes | 6 | 36 |
| UNIVERS-Surface_mounted_W800_H950_D165_36_Modular_Spacing-FWB63A | {"ObjectGuid":"4b98beaf-e054-4bb3-81df-89b0e6f75c23","ModelGuid":"5a9c6bb8-e142-4675-a376-75949bd55e93","VariantGuid":"56f5493e-38e8-426c-b844-3c9ad9408968","Revision":"#6","VariantName":"UNIVERS-Surface_mounted_W800_H950_D165_36_Modular_Spacing-FWB63A"} | Aufputz | 800 mm  [stored 2.62467 ft] | 950 mm  [stored 3.1168 ft] | 161 mm  [stored 0.528215 ft] | 6 | 950 mm  [stored 3.1168 ft] | 800 mm  [stored 2.62467 ft] | 36 | No | mit Ausschnitt | No | No | 3 | FWB63A | 0 | 0 | Yes | Yes | 6 | 36 |
| UNIVERS-Surface_mounted_W800_H950_D165_36_Modular_Spacing-FWB63GS | {"ObjectGuid":"4b98beaf-e054-4bb3-81df-89b0e6f75c23","ModelGuid":"5a9c6bb8-e142-4675-a376-75949bd55e93","VariantGuid":"e21c6ca1-5716-4609-80a9-64f100460f22","Revision":"#6","VariantName":"UNIVERS-Surface_mounted_W800_H950_D165_36_Modular_Spacing-FWB63GS"} | Aufputz | 800 mm  [stored 2.62467 ft] | 950 mm  [stored 3.1168 ft] | 161 mm  [stored 0.528215 ft] | 6 | 950 mm  [stored 3.1168 ft] | 800 mm  [stored 2.62467 ft] | 36 | Yes | mit Ausschnitt | Yes | Yes | 3 | FWB63GS | 0 | 0 | Yes | Yes | 6 | 36 |
| UNIVERS-Surface_mounted_W800_H950_D165_36_Modular_Spacing-FWB63N | {"ObjectGuid":"4b98beaf-e054-4bb3-81df-89b0e6f75c23","ModelGuid":"5a9c6bb8-e142-4675-a376-75949bd55e93","VariantGuid":"ed1638cd-4024-41f3-9b22-d3095b908944","Revision":"#6","VariantName":"UNIVERS-Surface_mounted_W800_H950_D165_36_Modular_Spacing-FWB63N"} | Aufputz | 800 mm  [stored 2.62467 ft] | 950 mm  [stored 3.1168 ft] | 161 mm  [stored 0.528215 ft] | 6 | 950 mm  [stored 3.1168 ft] | 800 mm  [stored 2.62467 ft] | 36 | No | mit Ausschnitt | No | No | 3 | FWB63N | 0 | 2 | Yes | Yes | 6 | 36 |
| UNIVERS-Surface_mounted_W800_H950_D165_36_Modular_Spacing-FWB63N3 | {"ObjectGuid":"4b98beaf-e054-4bb3-81df-89b0e6f75c23","ModelGuid":"5a9c6bb8-e142-4675-a376-75949bd55e93","VariantGuid":"50a61a89-3eff-4b24-aa3a-85778ecccef8","Revision":"#6","VariantName":"UNIVERS-Surface_mounted_W800_H950_D165_36_Modular_Spacing-FWB63N3"} | Aufputz | 800 mm  [stored 2.62467 ft] | 950 mm  [stored 3.1168 ft] | 161 mm  [stored 0.528215 ft] | 6 | 950 mm  [stored 3.1168 ft] | 800 mm  [stored 2.62467 ft] | 36 | No | mit Ausschnitt | No | No | 3 | FWB63N3 | 0 | 2 | Yes | Yes | 6 | 36 |
| UNIVERS-Surface_mounted_W800_H950_D165_36_Modular_Spacing-FWB63P | {"ObjectGuid":"4b98beaf-e054-4bb3-81df-89b0e6f75c23","ModelGuid":"5a9c6bb8-e142-4675-a376-75949bd55e93","VariantGuid":"ef2df2ce-28c4-4ac7-8a5c-db086a1dd930","Revision":"#6","VariantName":"UNIVERS-Surface_mounted_W800_H950_D165_36_Modular_Spacing-FWB63P"} | Aufputz | 800 mm  [stored 2.62467 ft] | 950 mm  [stored 3.1168 ft] | 161 mm  [stored 0.528215 ft] | 6 | 950 mm  [stored 3.1168 ft] | 800 mm  [stored 2.62467 ft] | 36 | No | geschlossen | No | No | 3 | FWB63P | 0 | 0 | Yes | No | 6 | 36 |
| UNIVERS-Surface_mounted_W800_H950_D165_36_Modular_Spacing-FWB63S | {"ObjectGuid":"4b98beaf-e054-4bb3-81df-89b0e6f75c23","ModelGuid":"5a9c6bb8-e142-4675-a376-75949bd55e93","VariantGuid":"c09c0441-569d-4c72-8eee-47bf01466d00","Revision":"#6","VariantName":"UNIVERS-Surface_mounted_W800_H950_D165_36_Modular_Spacing-FWB63S"} | Aufputz | 800 mm  [stored 2.62467 ft] | 950 mm  [stored 3.1168 ft] | 161 mm  [stored 0.528215 ft] | 6 | 950 mm  [stored 3.1168 ft] | 800 mm  [stored 2.62467 ft] | 36 | No | mit Ausschnitt | Yes | Yes | 3 | FWB63S | 0 | 0 | Yes | Yes | 6 | 36 |
| UNIVERS-Surface_mounted_W1050_H950_D165_48_Modular_Spacing-FWB64 | {"ObjectGuid":"4b98beaf-e054-4bb3-81df-89b0e6f75c23","ModelGuid":"5a9c6bb8-e142-4675-a376-75949bd55e93","VariantGuid":"f0d3a43e-528a-44f6-8f6c-9bc0a2ed9689","Revision":"#6","VariantName":"UNIVERS-Surface_mounted_W1050_H950_D165_48_Modular_Spacing-FWB64"} | Aufputz | 1050 mm | 950 mm  [stored 3.1168 ft] | 161 mm  [stored 0.528215 ft] | 6 | 950 mm  [stored 3.1168 ft] | 1050 mm | 48 | No | mit Ausschnitt | No | Yes | 4 | FWB64 | 0 | 0 | Yes | No | 6 | 48 |
| UNIVERS-Surface_mounted_W1050_H950_D165_48_Modular_Spacing-FWB64A | {"ObjectGuid":"4b98beaf-e054-4bb3-81df-89b0e6f75c23","ModelGuid":"5a9c6bb8-e142-4675-a376-75949bd55e93","VariantGuid":"4dae4cbd-edfc-4ddb-825a-dcfd6ab82fd9","Revision":"#6","VariantName":"UNIVERS-Surface_mounted_W1050_H950_D165_48_Modular_Spacing-FWB64A"} | Aufputz | 1050 mm | 950 mm  [stored 3.1168 ft] | 161 mm  [stored 0.528215 ft] | 6 | 950 mm  [stored 3.1168 ft] | 1050 mm | 48 | No | mit Ausschnitt | No | No | 4 | FWB64A | 0 | 0 | Yes | No | 6 | 48 |
| UNIVERS-Surface_mounted_W1050_H950_D165_48_Modular_Spacing-FWB64GS | {"ObjectGuid":"4b98beaf-e054-4bb3-81df-89b0e6f75c23","ModelGuid":"5a9c6bb8-e142-4675-a376-75949bd55e93","VariantGuid":"23523989-1c1b-4f40-87d0-0b0d13e6f30e","Revision":"#6","VariantName":"UNIVERS-Surface_mounted_W1050_H950_D165_48_Modular_Spacing-FWB64GS"} | Aufputz | 1050 mm | 950 mm  [stored 3.1168 ft] | 161 mm  [stored 0.528215 ft] | 6 | 950 mm  [stored 3.1168 ft] | 1050 mm | 48 | Yes | mit Ausschnitt | Yes | Yes | 4 | FWB64GS | 0 | 0 | Yes | No | 6 | 48 |
| UNIVERS-Surface_mounted_W1050_H950_D165_48_Modular_Spacing-FWB64N | {"ObjectGuid":"4b98beaf-e054-4bb3-81df-89b0e6f75c23","ModelGuid":"5a9c6bb8-e142-4675-a376-75949bd55e93","VariantGuid":"59f3e661-2c53-438f-9348-ec74ac9c31ab","Revision":"#6","VariantName":"UNIVERS-Surface_mounted_W1050_H950_D165_48_Modular_Spacing-FWB64N"} | Aufputz | 1050 mm | 950 mm  [stored 3.1168 ft] | 161 mm  [stored 0.528215 ft] | 6 | 950 mm  [stored 3.1168 ft] | 1050 mm | 48 | No | mit Ausschnitt | No | No | 4 | FWB64N | 0 | 2 | Yes | No | 6 | 48 |
| UNIVERS-Surface_mounted_W1050_H950_D165_48_Modular_Spacing-FWB64N3 | {"ObjectGuid":"4b98beaf-e054-4bb3-81df-89b0e6f75c23","ModelGuid":"5a9c6bb8-e142-4675-a376-75949bd55e93","VariantGuid":"8c0878c0-1dd8-4297-a977-b8d6d491558a","Revision":"#6","VariantName":"UNIVERS-Surface_mounted_W1050_H950_D165_48_Modular_Spacing-FWB64N3"} | Aufputz | 1050 mm | 950 mm  [stored 3.1168 ft] | 161 mm  [stored 0.528215 ft] | 6 | 950 mm  [stored 3.1168 ft] | 1050 mm | 48 | No | mit Ausschnitt | No | No | 4 | FWB64N3 | 0 | 2 | Yes | No | 6 | 48 |
| UNIVERS-Surface_mounted_W1050_H950_D165_48_Modular_Spacing-FWB64P | {"ObjectGuid":"4b98beaf-e054-4bb3-81df-89b0e6f75c23","ModelGuid":"5a9c6bb8-e142-4675-a376-75949bd55e93","VariantGuid":"9901c677-786d-4b9f-93a8-c7b5131efa41","Revision":"#6","VariantName":"UNIVERS-Surface_mounted_W1050_H950_D165_48_Modular_Spacing-FWB64P"} | Aufputz | 1050 mm | 950 mm  [stored 3.1168 ft] | 161 mm  [stored 0.528215 ft] | 6 | 950 mm  [stored 3.1168 ft] | 1050 mm | 48 | No | geschlossen | No | No | 4 | FWB64P | 0 | 0 | Yes | No | 6 | 48 |
| UNIVERS-Surface_mounted_W1050_H950_D165_48_Modular_Spacing-FWB64S | {"ObjectGuid":"4b98beaf-e054-4bb3-81df-89b0e6f75c23","ModelGuid":"5a9c6bb8-e142-4675-a376-75949bd55e93","VariantGuid":"123b6c66-5a00-4e00-9ad5-fff6dcad4456","Revision":"#6","VariantName":"UNIVERS-Surface_mounted_W1050_H950_D165_48_Modular_Spacing-FWB64S"} | Aufputz | 1050 mm | 950 mm  [stored 3.1168 ft] | 161 mm  [stored 0.528215 ft] | 6 | 950 mm  [stored 3.1168 ft] | 1050 mm | 48 | No | mit Ausschnitt | Yes | Yes | 4 | FWB64S | 0 | 0 | Yes | No | 6 | 48 |
| UNIVERS-Surface_mounted_W300_H1100_D165_12_Modular_Spacing-FWB71 | {"ObjectGuid":"4b98beaf-e054-4bb3-81df-89b0e6f75c23","ModelGuid":"5a9c6bb8-e142-4675-a376-75949bd55e93","VariantGuid":"4c4d5843-3160-4a99-b95d-586deb7e98e7","Revision":"#6","VariantName":"UNIVERS-Surface_mounted_W300_H1100_D165_12_Modular_Spacing-FWB71"} | Aufputz | 300 mm | 1100 mm | 161 mm  [stored 0.528215 ft] | 7 | 1100 mm | 300 mm | 12 | No | mit Ausschnitt | No | Yes | 1 | FWB71 | 0 | 0 | No | No | 7 | 12 |
| UNIVERS-Surface_mounted_W300_H1100_D165_12_Modular_Spacing-FWB71A | {"ObjectGuid":"4b98beaf-e054-4bb3-81df-89b0e6f75c23","ModelGuid":"5a9c6bb8-e142-4675-a376-75949bd55e93","VariantGuid":"04fcbcd4-b97d-4fa9-9a7b-0298753d3ba6","Revision":"#6","VariantName":"UNIVERS-Surface_mounted_W300_H1100_D165_12_Modular_Spacing-FWB71A"} | Aufputz | 300 mm | 1100 mm | 161 mm  [stored 0.528215 ft] | 7 | 1100 mm | 300 mm | 12 | No | mit Ausschnitt | No | No | 1 | FWB71A | 0 | 0 | No | No | 7 | 12 |
| UNIVERS-Surface_mounted_W300_H1100_D165_12_Modular_Spacing-FWB71GS | {"ObjectGuid":"4b98beaf-e054-4bb3-81df-89b0e6f75c23","ModelGuid":"5a9c6bb8-e142-4675-a376-75949bd55e93","VariantGuid":"9cfea633-9ca0-468a-98b1-3064db737663","Revision":"#6","VariantName":"UNIVERS-Surface_mounted_W300_H1100_D165_12_Modular_Spacing-FWB71GS"} | Aufputz | 300 mm | 1100 mm | 161 mm  [stored 0.528215 ft] | 7 | 1100 mm | 300 mm | 12 | Yes | mit Ausschnitt | Yes | Yes | 1 | FWB71GS | 0 | 0 | No | No | 7 | 12 |
| UNIVERS-Surface_mounted_W300_H1100_D165_12_Modular_Spacing-FWB71S | {"ObjectGuid":"4b98beaf-e054-4bb3-81df-89b0e6f75c23","ModelGuid":"5a9c6bb8-e142-4675-a376-75949bd55e93","VariantGuid":"c3c44fb0-8ee9-4e79-8d21-47ef95838725","Revision":"#6","VariantName":"UNIVERS-Surface_mounted_W300_H1100_D165_12_Modular_Spacing-FWB71S"} | Aufputz | 300 mm | 1100 mm | 161 mm  [stored 0.528215 ft] | 7 | 1100 mm | 300 mm | 12 | No | mit Ausschnitt | Yes | Yes | 1 | FWB71S | 0 | 0 | No | No | 7 | 12 |
| UNIVERS-Surface_mounted_W550_H1100_D165_24_Modular_Spacing-FWB72 | {"ObjectGuid":"4b98beaf-e054-4bb3-81df-89b0e6f75c23","ModelGuid":"5a9c6bb8-e142-4675-a376-75949bd55e93","VariantGuid":"29a57bc2-b4f6-44a6-ba16-ae77d7f82a5c","Revision":"#6","VariantName":"UNIVERS-Surface_mounted_W550_H1100_D165_24_Modular_Spacing-FWB72"} | Aufputz | 550 mm | 1100 mm | 161 mm  [stored 0.528215 ft] | 7 | 1100 mm | 550 mm | 24 | No | mit Ausschnitt | No | Yes | 2 | FWB72 | 0 | 0 | No | No | 7 | 24 |
| UNIVERS-Surface_mounted_W550_H1100_D165_24_Modular_Spacing-FWB72A | {"ObjectGuid":"4b98beaf-e054-4bb3-81df-89b0e6f75c23","ModelGuid":"5a9c6bb8-e142-4675-a376-75949bd55e93","VariantGuid":"45ae1708-9dbf-4b02-abc6-fa2e6d4a1877","Revision":"#6","VariantName":"UNIVERS-Surface_mounted_W550_H1100_D165_24_Modular_Spacing-FWB72A"} | Aufputz | 550 mm | 1100 mm | 161 mm  [stored 0.528215 ft] | 7 | 1100 mm | 550 mm | 24 | No | mit Ausschnitt | No | No | 2 | FWB72A | 0 | 0 | No | No | 7 | 24 |
| UNIVERS-Surface_mounted_W550_H1100_D165_24_Modular_Spacing-FWB72GS | {"ObjectGuid":"4b98beaf-e054-4bb3-81df-89b0e6f75c23","ModelGuid":"5a9c6bb8-e142-4675-a376-75949bd55e93","VariantGuid":"39fcef56-f86d-442d-877d-964aa891c0db","Revision":"#6","VariantName":"UNIVERS-Surface_mounted_W550_H1100_D165_24_Modular_Spacing-FWB72GS"} | Aufputz | 550 mm | 1100 mm | 161 mm  [stored 0.528215 ft] | 7 | 1100 mm | 550 mm | 24 | Yes | mit Ausschnitt | Yes | Yes | 2 | FWB72GS | 0 | 0 | No | No | 7 | 24 |
| UNIVERS-Surface_mounted_W550_H1100_D165_24_Modular_Spacing-FWB72N | {"ObjectGuid":"4b98beaf-e054-4bb3-81df-89b0e6f75c23","ModelGuid":"5a9c6bb8-e142-4675-a376-75949bd55e93","VariantGuid":"2eb9854a-5eec-425e-85cd-bd2b5dae5d4e","Revision":"#6","VariantName":"UNIVERS-Surface_mounted_W550_H1100_D165_24_Modular_Spacing-FWB72N"} | Aufputz | 550 mm | 1100 mm | 161 mm  [stored 0.528215 ft] | 7 | 1100 mm | 550 mm | 24 | No | mit Ausschnitt | No | No | 2 | FWB72N | 0 | 2 | No | No | 7 | 24 |
| UNIVERS-Surface_mounted_W550_H1100_D165_24_Modular_Spacing-FWB72N3 | {"ObjectGuid":"4b98beaf-e054-4bb3-81df-89b0e6f75c23","ModelGuid":"5a9c6bb8-e142-4675-a376-75949bd55e93","VariantGuid":"4cafc93b-204e-4207-b5a8-98482d2c7c3f","Revision":"#6","VariantName":"UNIVERS-Surface_mounted_W550_H1100_D165_24_Modular_Spacing-FWB72N3"} | Aufputz | 550 mm | 1100 mm | 161 mm  [stored 0.528215 ft] | 7 | 1100 mm | 550 mm | 24 | No | mit Ausschnitt | No | No | 2 | FWB72N3 | 0 | 2 | No | No | 7 | 24 |
| UNIVERS-Surface_mounted_W550_H1100_D165_24_Modular_Spacing-FWB72S | {"ObjectGuid":"4b98beaf-e054-4bb3-81df-89b0e6f75c23","ModelGuid":"5a9c6bb8-e142-4675-a376-75949bd55e93","VariantGuid":"e4df02f0-17e3-451e-8eec-14f42237c94d","Revision":"#6","VariantName":"UNIVERS-Surface_mounted_W550_H1100_D165_24_Modular_Spacing-FWB72S"} | Aufputz/Unterputz | 550 mm | 1100 mm | 161 mm  [stored 0.528215 ft] | 7 | 1100 mm | 550 mm | 24 | No | mit Ausschnitt | Yes | Yes | 2 | FWB72S | 0 | 0 | No | No | 7 | 24 |

note: [stored X ft] marks values corroborated as IEEE doubles in the binary element streams (Revit-internal decimal feet)

## geometry (parser evidence)
native form markers: Sweep x12
no freeform markers — native parametric forms only
